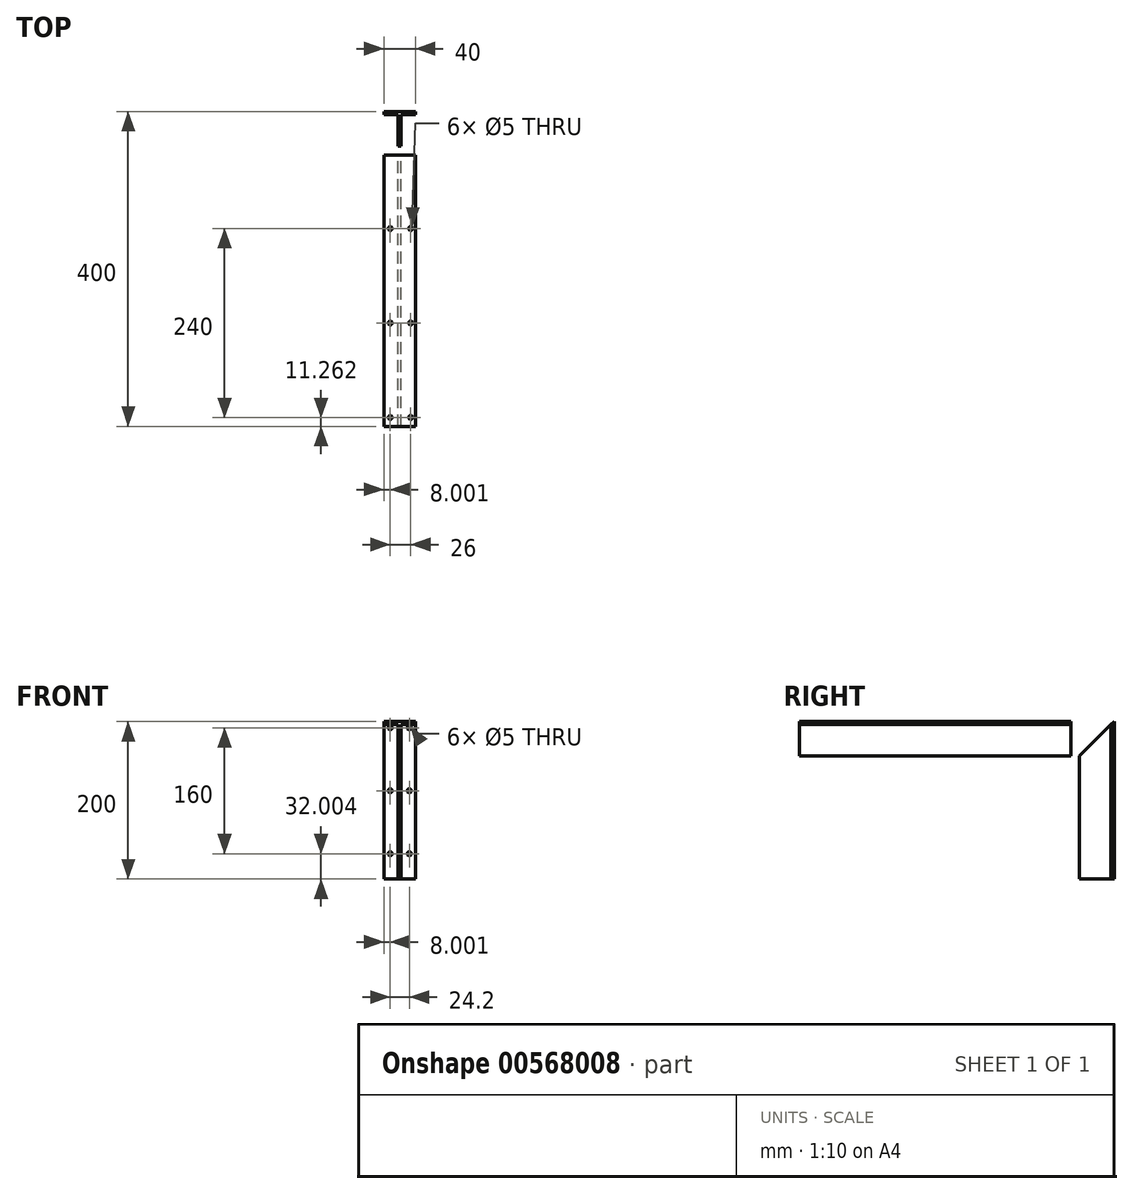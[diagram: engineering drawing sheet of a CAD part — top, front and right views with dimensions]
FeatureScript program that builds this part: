
annotation { "Feature Type Name" : "Feature", "Feature Type Description" : "" }
export const myFeature = defineFeature(function(context is Context, id is Id, definition is map)
    precondition{}
    {
        {
            var Q0;
            Q0=qCreatedBy(makeId("Front.planeOp"),FACE);
            var sketch = newSketch(context, id + "F0", { "sketchPlane" : qUnion([Q0])});
            skLineSegment(sketch, "E0.bottom", {"start": v(-21.49, 24.71) * mm, "end": v(18.51, 24.71) * mm});
            skLineSegment(sketch, "E0.top", {"start": v(-21.49, 20.71) * mm, "end": v(-3.49, 20.71) * mm});
            skLineSegment(sketch, "E0.left", {"start": v(-21.49, 24.71) * mm, "end": v(-21.49, 20.71) * mm});
            skLineSegment(sketch, "E0.right", {"start": v(18.51, 24.71) * mm, "end": v(18.51, 20.71) * mm});
            skLineSegment(sketch, "E1.bottom", {"start": v(-3.49, 20.71) * mm, "end": v(0.51, 20.71) * mm});
            skLineSegment(sketch, "E1.top", {"start": v(-3.49, -19.29) * mm, "end": v(0.51, -19.29) * mm});
            skLineSegment(sketch, "E1.left", {"start": v(-3.49, 20.71) * mm, "end": v(-3.49, -19.29) * mm});
            skLineSegment(sketch, "E1.right", {"start": v(0.51, 20.71) * mm, "end": v(0.51, -19.29) * mm});
            skLineSegment(sketch, "E2", {"start": v(0.51, 20.71) * mm, "end": v(0.51, 20.71) * mm});
            skLineSegment(sketch, "E3", {"start": v(0.51, 20.71) * mm, "end": v(18.51, 20.71) * mm});
            skSolve(sketch);
        }
        {
            var Q0;
            Q0 = qSketchRegion(id + "F0", true);
            extrude(context, id + "F1", {"entities" : qUnion([Q0]), "endBound" : BoundingType.SYMMETRIC, "depth" : 400 * mm, "offsetDistance" : 25 * mm});
        }
        {
            var Q0;
            Q0=makeQuery(id+"F1.opExtrude","SWEPT_FACE",FACE,{"disambiguationData":[OSD([sQuery(id+"F0.wireOp",EDGE,"E0.left")])]});
            var sketch = newSketch(context, id + "F2", { "sketchPlane" : qUnion([Q0])});
            skLineSegment(sketch, "E4", {"start": v(-200, 24.71) * mm, "end": v(-107.67, -67.62) * mm});
            skLineSegment(sketch, "E5", {"start": v(-107.67, -67.62) * mm, "end": v(-200, -67.62) * mm});
            skLineSegment(sketch, "E6", {"start": v(-200, -67.62) * mm, "end": v(-200, 24.71) * mm});
            skSolve(sketch);
        }
        {
            var Q0;
            {var subQ0=sQuery(id+"F2.wireOp",EDGE,"E5");Q0=makeQuery(id+"F2.imprint","IMPRINT",FACE,{"disambiguationData":[TD([[makeQuery(id+"F2.imprint","IMPRINT",EDGE,{"derivedFrom":subQ0}),-1.0]])]});}
            var Q1;
            {var subQ1=sQuery(id+"F2.wireOp",EDGE,"E4");var subQ2=sQuery(id+"F0.wireOp",EDGE,"E0.left");var subQ4=makeQuery(id+"F1.opExtrude","SWEPT_EDGE",EDGE,{"disambiguationData":[OSD([sQuery(id+"F0.wireOp",EDGE,"E0.top"),subQ2])]});var subQ5=makeQuery(id+"F2.imprint","INTERSECT",VERTEX,{"derivedFrom":[subQ4,subQ1]});Q1=makeQuery(id+"F2.imprint","IMPRINT",FACE,{"disambiguationData":[TD([[makeQuery(id+"F2.imprint","IMPRINT",EDGE,{"disambiguationData":[TD([[subQ5,1.0]])],"derivedFrom":subQ1}),-1.0]])]});}
            extrude(context, id + "F3", {"entities" : qUnion([Q0, Q1]), "operationType" : NewBodyOperationType.REMOVE, "endBound" : BoundingType.SYMMETRIC, "oppositeDirection" : true, "depth" : 103.8 * mm, "offsetDistance" : 25 * mm});
        }
        {
            var Q0;
            Q0=makeQuery(id+"F1.opExtrude","SWEPT_FACE",FACE,{"disambiguationData":[OSD([sQuery(id+"F0.wireOp",EDGE,"E0.bottom")])]});
            var sketch = newSketch(context, id + "F4", { "sketchPlane" : qUnion([Q0])});
            skLineSegment(sketch, "E7.bottom", {"start": v(-21.49, 200) * mm, "end": v(18.51, 200) * mm});
            skLineSegment(sketch, "E7.top", {"start": v(-21.49, 196) * mm, "end": v(-3.49, 196) * mm});
            skLineSegment(sketch, "E7.left", {"start": v(-21.49, 200) * mm, "end": v(-21.49, 196) * mm});
            skLineSegment(sketch, "E7.right", {"start": v(18.51, 200) * mm, "end": v(18.51, 196) * mm});
            skLineSegment(sketch, "E8.bottom", {"start": v(-3.49, 196) * mm, "end": v(0.51, 196) * mm});
            skLineSegment(sketch, "E8.top", {"start": v(-3.49, 156) * mm, "end": v(0.51, 156) * mm});
            skLineSegment(sketch, "E8.left", {"start": v(-3.49, 196) * mm, "end": v(-3.49, 156) * mm});
            skLineSegment(sketch, "E8.right", {"start": v(0.51, 196) * mm, "end": v(0.51, 156) * mm});
            skLineSegment(sketch, "E9", {"start": v(0.51, 196) * mm, "end": v(18.51, 196) * mm});
            skSolve(sketch);
        }
        {
            var Q0;
            Q0=makeQuery(id+"F4.imprint","IMPRINT",FACE,{"disambiguationData":[TD([[makeQuery(id+"F4.imprint","IMPRINT",EDGE,{"derivedFrom":sQuery(id+"F4.wireOp",EDGE,"E7.bottom")}),-1.0]])]});
            var Q1;
            Q1=makeQuery(id+"F4.imprint","IMPRINT",FACE,{"disambiguationData":[TD([[makeQuery(id+"F4.imprint","IMPRINT",EDGE,{"derivedFrom":sQuery(id+"F4.wireOp",EDGE,"E8.top")}),1.0]])]});
            extrude(context, id + "F5", {"entities" : qUnion([Q0, Q1]), "oppositeDirection" : true, "depth" : 200 * mm, "offsetDistance" : 25 * mm});
        }
        {
            var Q0;
            Q0=makeQuery(id+"F5.opExtrude","SWEPT_FACE",FACE,{"disambiguationData":[OSD([sQuery(id+"F4.wireOp",EDGE,"E7.left")])]});
            var sketch = newSketch(context, id + "F6", { "sketchPlane" : qUnion([Q0])});
            skLineSegment(sketch, "E10", {"start": v(-200, 24.71) * mm, "end": v(-144.82, -30.47) * mm});
            skLineSegment(sketch, "E11", {"start": v(-144.82, -30.47) * mm, "end": v(-144.82, 24.71) * mm});
            skLineSegment(sketch, "E12", {"start": v(-144.82, 24.71) * mm, "end": v(-200, 24.71) * mm});
            skSolve(sketch);
        }
        {
            var Q0;
            {var subQ0=sQuery(id+"F6.wireOp",EDGE,"E11");Q0=makeQuery(id+"F6.imprint","IMPRINT",FACE,{"disambiguationData":[TD([[makeQuery(id+"F6.imprint","IMPRINT",EDGE,{"derivedFrom":subQ0}),1.0]])]});}
            var Q1;
            {var subQ0=sQuery(id+"F6.wireOp",EDGE,"E12");var subQ1=sQuery(id+"F6.wireOp",EDGE,"E10");var subQ2=sQuery(id+"F4.wireOp",EDGE,"E7.left");var subQ3=makeQuery(id+"F6.imprint","INTERSECT",VERTEX,{"derivedFrom":[makeQuery(id+"F5.opExtrude","SWEPT_EDGE",EDGE,{"disambiguationData":[OSD([sQuery(id+"F4.wireOp",EDGE,"E7.bottom"),subQ2])]}),subQ1,subQ0]});Q1=makeQuery(id+"F6.imprint","IMPRINT",FACE,{"disambiguationData":[TD([[makeQuery(id+"F6.imprint","IMPRINT",EDGE,{"disambiguationData":[TD([[subQ3,-1.0]])],"derivedFrom":subQ1}),1.0]])]});}
            extrude(context, id + "F7", {"entities" : qUnion([Q0, Q1]), "operationType" : NewBodyOperationType.REMOVE, "oppositeDirection" : true, "depth" : 41.7 * mm, "offsetDistance" : 25 * mm});
        }
        {
            var Q0;
            Q0=makeQuery(id+"F1.opExtrude","SWEPT_FACE",FACE,{"disambiguationData":[OSD([sQuery(id+"F0.wireOp",EDGE,"E0.bottom")])]});
            var sketch = newSketch(context, id + "F8", { "sketchPlane" : qUnion([Q0])});
            skCircle(sketch, "E13", {"center": v(-13.49, -188.74) * mm, "radius": 2.13 * mm});
            skCircle(sketch, "E14.0.1.0", {"center": v(-13.49, -68.74) * mm, "radius": 2.13 * mm});
            skCircle(sketch, "E14.0.2.0", {"center": v(-13.49, 51.26) * mm, "radius": 2.13 * mm});
            skCircle(sketch, "E14.0.3.0", {"center": v(-13.49, 171.26) * mm, "radius": 2.13 * mm});
            skCircle(sketch, "E14.1.0.0", {"center": v(12.51, -188.74) * mm, "radius": 2.13 * mm});
            skCircle(sketch, "E14.1.1.0", {"center": v(12.51, -68.74) * mm, "radius": 2.13 * mm});
            skCircle(sketch, "E14.1.2.0", {"center": v(12.51, 51.26) * mm, "radius": 2.13 * mm});
            skCircle(sketch, "E14.1.3.0", {"center": v(12.51, 171.26) * mm, "radius": 2.13 * mm});
            skLineSegment(sketch, "E14.direction1", {"start": v(-13.49, -188.74) * mm, "end": v(12.51, -188.74) * mm, "construction": true});
            skLineSegment(sketch, "E14.direction2", {"start": v(-13.49, -188.74) * mm, "end": v(-13.49, -68.74) * mm, "construction": true});
            skSolve(sketch);
        }
        {
            var Q0;
            Q0=sQuery(id+"F8.wireOp",VERTEX,"E14.0.3.0.center");
            var Q1;
            Q1=sQuery(id+"F8.wireOp",VERTEX,"E14.1.3.0.center");
            var Q2;
            Q2=sQuery(id+"F8.wireOp",VERTEX,"E14.1.2.0.center");
            var Q3;
            Q3=sQuery(id+"F8.wireOp",VERTEX,"E14.0.2.0.center");
            var Q4;
            Q4=sQuery(id+"F8.wireOp",VERTEX,"E14.0.1.0.center");
            var Q5;
            Q5=sQuery(id+"F8.wireOp",VERTEX,"E14.1.1.0.center");
            var Q6;
            Q6=sQuery(id+"F8.wireOp",VERTEX,"E13.center");
            var Q7;
            Q7=sQuery(id+"F8.wireOp",VERTEX,"E14.1.0.0.center");
            var Q8;
            Q8=makeQuery(id+"F1.opExtrude","SWEPT_BODY",BODY,{"disambiguationData":[OSD([sQuery(id+"F0.wireOp",EDGE,"E0.bottom"),sQuery(id+"F0.wireOp",EDGE,"E0.top"),sQuery(id+"F0.wireOp",EDGE,"E0.left"),sQuery(id+"F0.wireOp",EDGE,"E0.right"),sQuery(id+"F0.wireOp",EDGE,"E1.top"),sQuery(id+"F0.wireOp",EDGE,"E1.left"),sQuery(id+"F0.wireOp",EDGE,"E1.right"),sQuery(id+"F0.wireOp",EDGE,"E3")])]});
            hole(context, id + "F9", {"style" : HoleStyle.SIMPLE, "endStyle" : HoleEndStyle.THROUGH, "holeDiameter" : 5 * mm, "isTappedThrough" : true, "tappedDepth" : 12 * mm, "tapClearance" : 3, "locations" : qUnion([Q0, Q1, Q2, Q3, Q4, Q5, Q6, Q7]), "scope" : qUnion([Q8])});
        }
        {
            var Q0;
            Q0=makeQuery(id+"F5.opExtrude","SWEPT_FACE",FACE,{"disambiguationData":[OSD([sQuery(id+"F4.wireOp",EDGE,"E7.bottom")])]});
            var sketch = newSketch(context, id + "F10", { "sketchPlane" : qUnion([Q0])});
            skPoint(sketch, "E15", {"position": v(-12.51, -166.94) * mm});
            skCircle(sketch, "E16", {"center": v(13.49, 16.71) * mm, "radius": 2.27 * mm});
            skCircle(sketch, "E17.0.1.0", {"center": v(13.49, -63.29) * mm, "radius": 2.27 * mm});
            skCircle(sketch, "E17.0.2.0", {"center": v(13.49, -143.29) * mm, "radius": 2.27 * mm});
            skCircle(sketch, "E17.1.0.0", {"center": v(-10.71, 16.71) * mm, "radius": 2.27 * mm});
            skCircle(sketch, "E17.1.1.0", {"center": v(-10.71, -63.29) * mm, "radius": 2.27 * mm});
            skCircle(sketch, "E17.1.2.0", {"center": v(-10.71, -143.29) * mm, "radius": 2.27 * mm});
            skLineSegment(sketch, "E17.direction1", {"start": v(13.49, 16.71) * mm, "end": v(-10.71, 16.71) * mm, "construction": true});
            skLineSegment(sketch, "E17.direction2", {"start": v(13.49, 16.71) * mm, "end": v(13.49, -63.29) * mm, "construction": true});
            skSolve(sketch);
        }
        {
            var Q0;
            Q0=sQuery(id+"F10.wireOp",VERTEX,"E17.direction1.end");
            var Q1;
            Q1=sQuery(id+"F10.wireOp",VERTEX,"E17.direction2.start");
            var Q2;
            Q2=sQuery(id+"F10.wireOp",VERTEX,"E17.direction2.end");
            var Q3;
            Q3=sQuery(id+"F10.wireOp",VERTEX,"E17.1.1.0.center");
            var Q4;
            Q4=sQuery(id+"F10.wireOp",VERTEX,"E17.1.2.0.center");
            var Q5;
            Q5=sQuery(id+"F10.wireOp",VERTEX,"E17.0.2.0.center");
            var Q6;
            Q6=makeQuery(id+"F5.opExtrude","SWEPT_BODY",BODY,{"disambiguationData":[OSD([sQuery(id+"F4.wireOp",EDGE,"E7.bottom"),sQuery(id+"F4.wireOp",EDGE,"E7.top"),sQuery(id+"F4.wireOp",EDGE,"E7.left"),sQuery(id+"F4.wireOp",EDGE,"E7.right"),sQuery(id+"F4.wireOp",EDGE,"E8.top"),sQuery(id+"F4.wireOp",EDGE,"E8.left"),sQuery(id+"F4.wireOp",EDGE,"E8.right"),sQuery(id+"F4.wireOp",EDGE,"E9")])]});
            hole(context, id + "F11", {"style" : HoleStyle.SIMPLE, "endStyle" : HoleEndStyle.THROUGH, "holeDiameter" : 5 * mm, "isTappedThrough" : true, "tappedDepth" : 12 * mm, "tapClearance" : 3, "locations" : qUnion([Q0, Q1, Q2, Q3, Q4, Q5]), "scope" : qUnion([Q6])});
        }
    });
